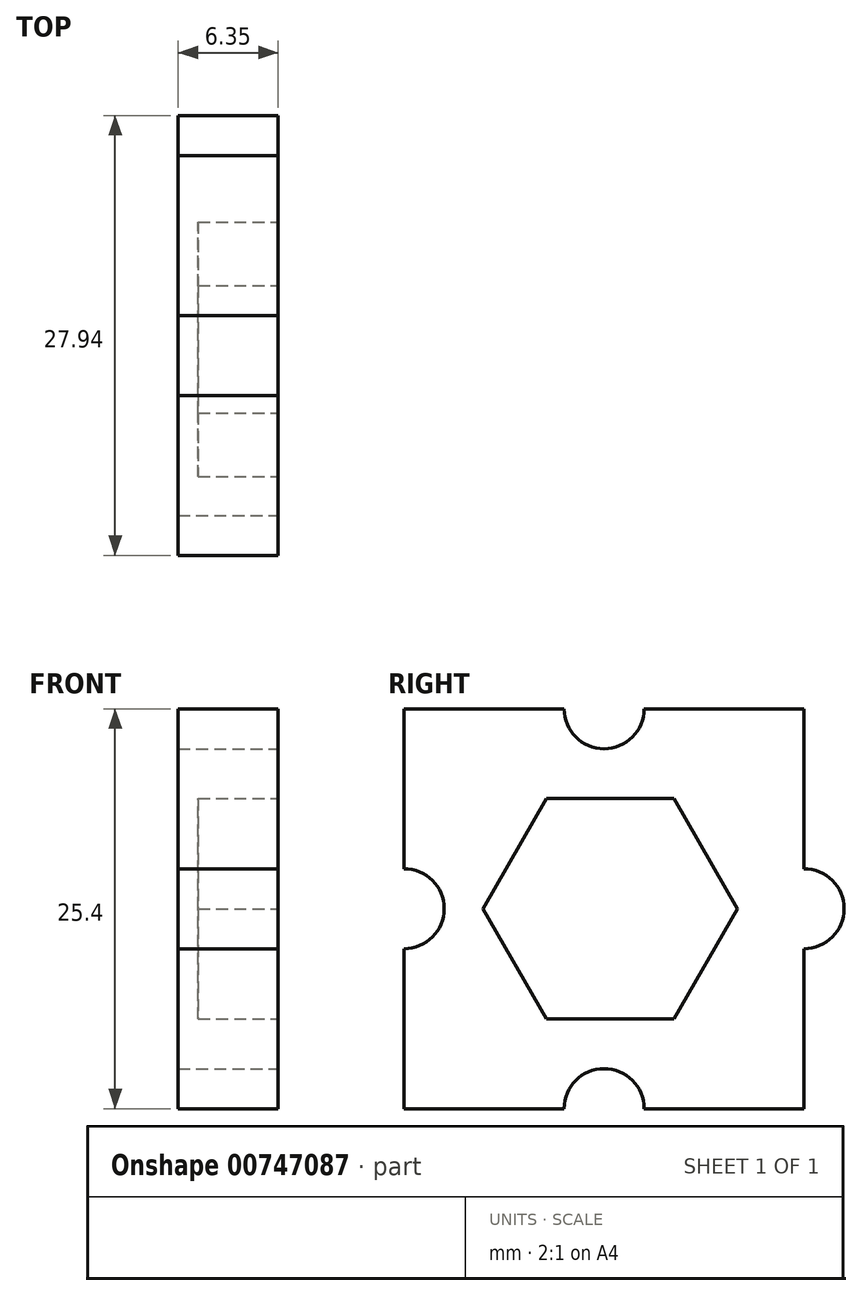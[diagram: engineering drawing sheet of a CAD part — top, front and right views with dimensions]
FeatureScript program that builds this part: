
annotation { "Feature Type Name" : "Feature", "Feature Type Description" : "" }
export const myFeature = defineFeature(function(context is Context, id is Id, definition is map)
    precondition{}
    {
        {
            var Q0;
            Q0=qCreatedBy(makeId("Right.planeOp"),FACE);
            var sketch = newSketch(context, id + "F0", { "sketchPlane" : qUnion([Q0])});
            skLineSegment(sketch, "E0", {"start": v(0, 0) * mm, "end": v(0, 25.4) * mm});
            skLineSegment(sketch, "E1", {"start": v(0, 25.4) * mm, "end": v(25.4, 25.4) * mm});
            skLineSegment(sketch, "E2", {"start": v(25.4, 25.4) * mm, "end": v(25.4, 0) * mm});
            skLineSegment(sketch, "E3", {"start": v(25.4, 0) * mm, "end": v(0, 0) * mm});
            skSolve(sketch);
        }
        {
            var Q0;
            Q0=qSketchRegion(id+"F0",true);
            extrude(context, id + "F1", {"entities" : qUnion([Q0]), "depth" : 6.35 * mm, "offsetDistance" : 25.4 * mm});
        }
        {
            var Q0;
            Q0=makeQuery(id+"F1.opExtrude","CAP_FACE",FACE,{"disambiguationData":[OSD([sQuery(id+"F0.wireOp",EDGE,"E0"),sQuery(id+"F0.wireOp",EDGE,"E1"),sQuery(id+"F0.wireOp",EDGE,"E2"),sQuery(id+"F0.wireOp",EDGE,"E3")])],"isStart":false});
            var sketch = newSketch(context, id + "F2", { "sketchPlane" : qUnion([Q0])});
            skCircle(sketch, "E4", {"center": v(12.7, 0) * mm, "radius": 2.54 * mm});
            skCircle(sketch, "E5", {"center": v(0, 12.7) * mm, "radius": 2.54 * mm});
            skCircle(sketch, "E6", {"center": v(12.7, 25.4) * mm, "radius": 2.54 * mm});
            skSolve(sketch);
        }
        {
            var Q0;
            Q0=qSketchRegion(id+"F2",true);
            extrude(context, id + "F3", {"entities" : qUnion([Q0]), "operationType" : NewBodyOperationType.REMOVE, "oppositeDirection" : true, "depth" : 6.35 * mm, "offsetDistance" : 25.4 * mm});
        }
        {
            var Q0;
            Q0=makeQuery(id+"F1.opExtrude","CAP_FACE",FACE,{"disambiguationData":[OSD([sQuery(id+"F0.wireOp",EDGE,"E0"),sQuery(id+"F0.wireOp",EDGE,"E1"),sQuery(id+"F0.wireOp",EDGE,"E2"),sQuery(id+"F0.wireOp",EDGE,"E3")])],"isStart":false});
            var sketch = newSketch(context, id + "F4", { "sketchPlane" : qUnion([Q0])});
            skCircle(sketch, "E7", {"center": v(25.4, 12.7) * mm, "radius": 2.54 * mm});
            skSolve(sketch);
        }
        {
            var Q0;
            Q0=qSketchRegion(id+"F4",true);
            extrude(context, id + "F5", {"entities" : qUnion([Q0]), "operationType" : NewBodyOperationType.ADD, "oppositeDirection" : true, "depth" : 6.35 * mm, "offsetDistance" : 25.4 * mm});
        }
        {
            var Q0;
            Q0=makeQuery(id+"F5.boolean.opBoolean","MERGE",FACE,{"derivedFrom":[makeQuery(id+"F1.opExtrude","CAP_FACE",FACE,{"disambiguationData":[OSD([sQuery(id+"F0.wireOp",EDGE,"E0"),sQuery(id+"F0.wireOp",EDGE,"E1"),sQuery(id+"F0.wireOp",EDGE,"E2"),sQuery(id+"F0.wireOp",EDGE,"E3")])],"isStart":false}),makeQuery(id+"F5.opExtrude","CAP_FACE",FACE,{"disambiguationData":[OSD([sQuery(id+"F4.wireOp",EDGE,"E7")])],"isStart":true})]});
            var sketch = newSketch(context, id + "F6", { "sketchPlane" : qUnion([Q0])});
            skCircle(sketch, "E8.cCircle", {"center": v(13.08, 12.7) * mm, "radius": 7 * mm, "construction": true});
            skLineSegment(sketch, "E8.0", {"start": v(17.13, 19.7) * mm, "end": v(21.17, 12.7) * mm});
            skLineSegment(sketch, "E8.1", {"start": v(21.17, 12.7) * mm, "end": v(17.12, 5.7) * mm});
            skLineSegment(sketch, "E8.2", {"start": v(17.12, 5.7) * mm, "end": v(9.04, 5.7) * mm});
            skLineSegment(sketch, "E8.3", {"start": v(9.04, 5.7) * mm, "end": v(5, 12.7) * mm});
            skLineSegment(sketch, "E8.4", {"start": v(5, 12.7) * mm, "end": v(9.04, 19.7) * mm});
            skLineSegment(sketch, "E8.5", {"start": v(9.04, 19.7) * mm, "end": v(17.13, 19.7) * mm});
            skPoint(sketch, "E8.0.midPoint", {"position": v(19.15, 16.2) * mm});
            skSolve(sketch);
        }
        {
            var Q0;
            Q0 = qSketchRegion(id + "F6", true);
            extrude(context, id + "F7", {"entities" : qUnion([Q0]), "operationType" : NewBodyOperationType.REMOVE, "oppositeDirection" : true, "depth" : 5.08 * mm, "offsetDistance" : 25.4 * mm});
        }
    });
